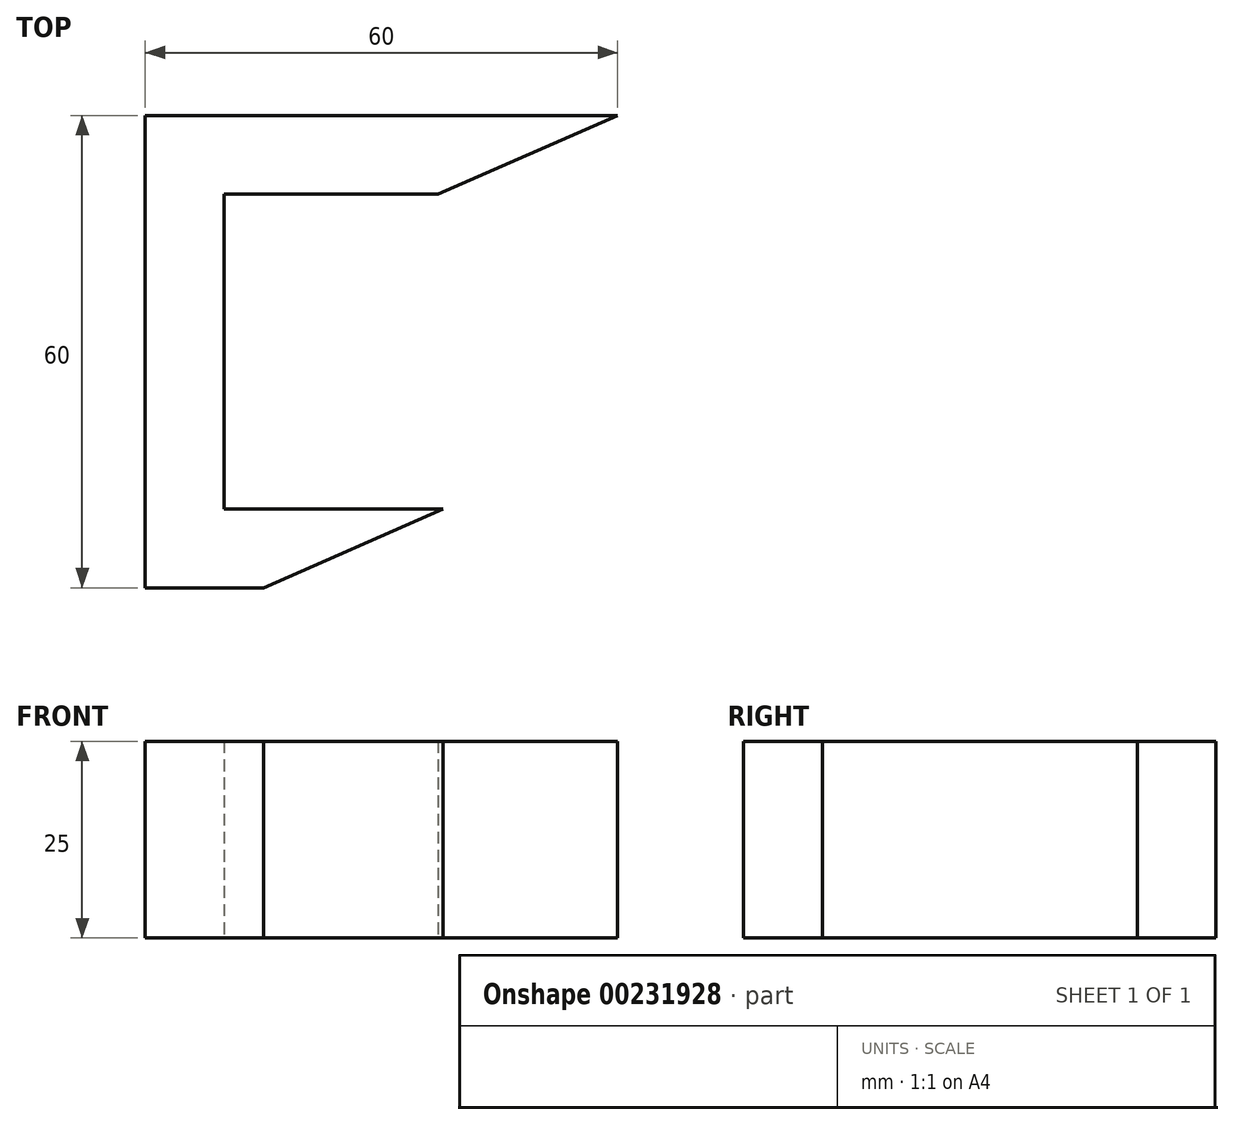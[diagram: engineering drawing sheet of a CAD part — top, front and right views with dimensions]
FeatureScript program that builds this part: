
annotation { "Feature Type Name" : "Feature", "Feature Type Description" : "" }
export const myFeature = defineFeature(function(context is Context, id is Id, definition is map)
    precondition{}
    {
        {
            var Q0;
            Q0=qCreatedBy(makeId("Top.planeOp"),FACE);
            var sketch = newSketch(context, id + "F0", { "sketchPlane" : qUnion([Q0])});
            skLineSegment(sketch, "E0", {"start": v(-60, -60) * mm, "end": v(-60, 0) * mm});
            skLineSegment(sketch, "E1", {"start": v(-60, 0) * mm, "end": v(0, 0) * mm});
            skLineSegment(sketch, "E2", {"start": v(0, 0) * mm, "end": v(-22.8, -10) * mm});
            skLineSegment(sketch, "E3", {"start": v(-22.8, -10) * mm, "end": v(-50, -10) * mm});
            skLineSegment(sketch, "E4", {"start": v(-50, -10) * mm, "end": v(-50, -50) * mm});
            skLineSegment(sketch, "E5", {"start": v(-45, -60) * mm, "end": v(-60, -60) * mm});
            skLineSegment(sketch, "E6", {"start": v(-22.2, -50) * mm, "end": v(-50, -50) * mm});
            skLineSegment(sketch, "E7", {"start": v(-22.2, -50) * mm, "end": v(-45, -60) * mm});
            skSolve(sketch);
        }
        {
            var Q0;
            Q0 = qSketchRegion(id + "F0", true);
            extrude(context, id + "F1", {"entities" : qUnion([Q0]), "depth" : 25 * mm});
        }
    });
